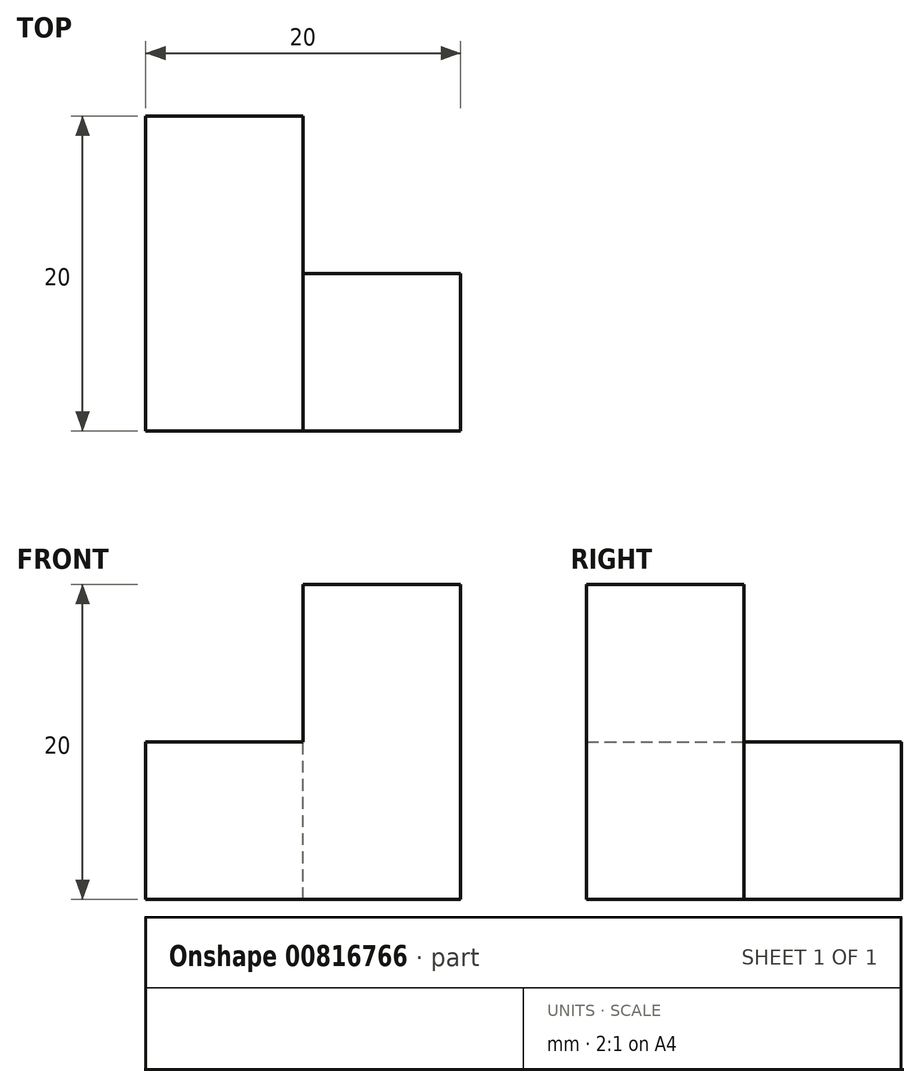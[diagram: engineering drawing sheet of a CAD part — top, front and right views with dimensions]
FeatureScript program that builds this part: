
annotation { "Feature Type Name" : "Feature", "Feature Type Description" : "" }
export const myFeature = defineFeature(function(context is Context, id is Id, definition is map)
    precondition{}
    {
        {
            var Q0;
            Q0=qCreatedBy(makeId("Top.planeOp"),FACE);
            var sketch = newSketch(context, id + "F0", { "sketchPlane" : qUnion([Q0])});
            skLineSegment(sketch, "E0.bottom", {"start": v(0, 0) * mm, "end": v(10, 0) * mm});
            skLineSegment(sketch, "E0.top", {"start": v(0, 10) * mm, "end": v(10, 10) * mm});
            skLineSegment(sketch, "E0.left", {"start": v(0, 0) * mm, "end": v(0, 10) * mm});
            skLineSegment(sketch, "E0.right", {"start": v(10, 0) * mm, "end": v(10, 10) * mm});
            skSolve(sketch);
        }
        {
            var Q0;
            Q0=makeQuery(id+"F0.imprint","IMPRINT",FACE,{"disambiguationData":[TD([[makeQuery(id+"F0.imprint","IMPRINT",EDGE,{"derivedFrom":sQuery(id+"F0.wireOp",EDGE,"E0.bottom")}),1.0]])]});
            extrude(context, id + "F1", {"entities" : qUnion([Q0]), "depth" : 20 * mm, "offsetDistance" : 25 * mm});
        }
        {
            var Q0;
            Q0=makeQuery(id+"F1.opExtrude","SWEPT_FACE",FACE,{"disambiguationData":[OSD([sQuery(id+"F0.wireOp",EDGE,"E0.left")])]});
            var sketch = newSketch(context, id + "F2", { "sketchPlane" : qUnion([Q0])});
            skLineSegment(sketch, "E1.bottom", {"start": v(0, 0) * mm, "end": v(-10, 0) * mm});
            skLineSegment(sketch, "E1.top", {"start": v(0, 10) * mm, "end": v(-10, 10) * mm});
            skLineSegment(sketch, "E1.left", {"start": v(0, 0) * mm, "end": v(0, 10) * mm});
            skLineSegment(sketch, "E1.right", {"start": v(-10, 0) * mm, "end": v(-10, 10) * mm});
            skSolve(sketch);
        }
        {
            var Q0;
            Q0=makeQuery(id+"F2.imprint","IMPRINT",FACE,{"disambiguationData":[TD([[makeQuery(id+"F2.imprint","IMPRINT",EDGE,{"derivedFrom":sQuery(id+"F2.wireOp",EDGE,"E1.bottom")}),-1.0]])]});
            extrude(context, id + "F3", {"entities" : qUnion([Q0]), "operationType" : NewBodyOperationType.ADD, "depth" : 10 * mm, "offsetDistance" : 25 * mm});
        }
        {
            var Q0;
            Q0=makeQuery(id+"F3.boolean.opBoolean","MERGE",FACE,{"derivedFrom":[makeQuery(id+"F1.opExtrude","SWEPT_FACE",FACE,{"disambiguationData":[OSD([sQuery(id+"F0.wireOp",EDGE,"E0.top")])]}),makeQuery(id+"F3.opExtrude","SWEPT_FACE",FACE,{"disambiguationData":[OSD([sQuery(id+"F2.wireOp",EDGE,"E1.right")])]})]});
            var sketch = newSketch(context, id + "F4", { "sketchPlane" : qUnion([Q0])});
            skLineSegment(sketch, "E2.bottom", {"start": v(0, 0) * mm, "end": v(10, 0) * mm});
            skLineSegment(sketch, "E2.top", {"start": v(0, 10) * mm, "end": v(10, 10) * mm});
            skLineSegment(sketch, "E2.left", {"start": v(0, 0) * mm, "end": v(0, 10) * mm});
            skLineSegment(sketch, "E2.right", {"start": v(10, 0) * mm, "end": v(10, 10) * mm});
            skSolve(sketch);
        }
        {
            var Q0;
            Q0=makeQuery(id+"F4.imprint","IMPRINT",FACE,{"disambiguationData":[TD([[makeQuery(id+"F4.imprint","IMPRINT",EDGE,{"derivedFrom":sQuery(id+"F4.wireOp",EDGE,"E2.bottom")}),-1.0]])]});
            extrude(context, id + "F5", {"entities" : qUnion([Q0]), "operationType" : NewBodyOperationType.ADD, "depth" : 10 * mm, "offsetDistance" : 25 * mm});
        }
    });
